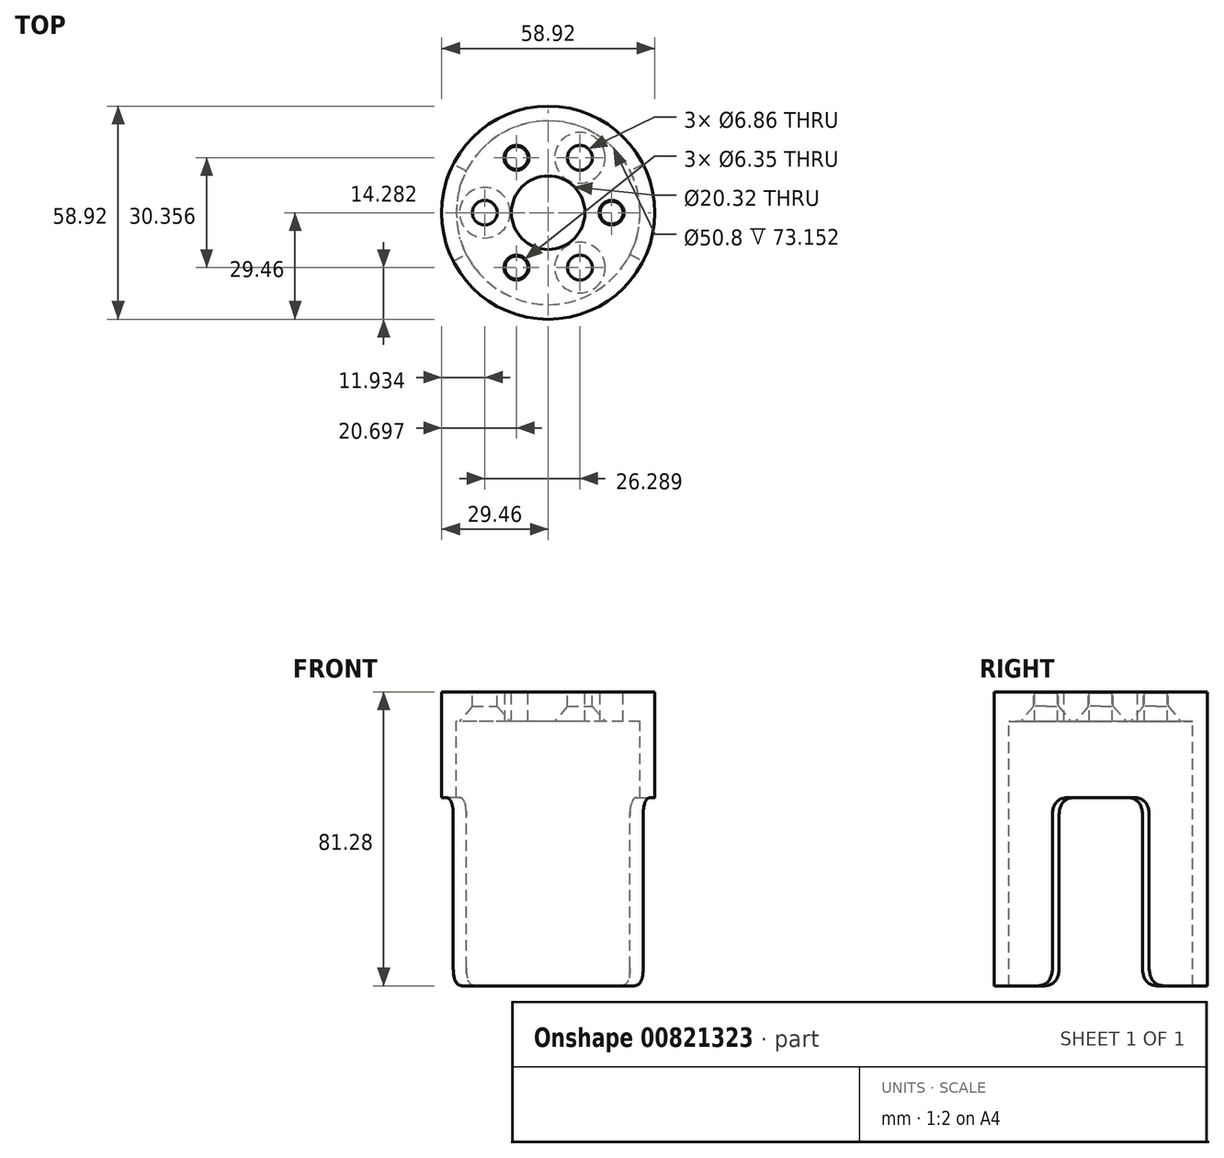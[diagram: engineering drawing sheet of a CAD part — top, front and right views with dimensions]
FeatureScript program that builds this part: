
annotation { "Feature Type Name" : "Feature", "Feature Type Description" : "" }
export const myFeature = defineFeature(function(context is Context, id is Id, definition is map)
    precondition{}
    {
        {
            var Q0;
            Q0=qCreatedBy(makeId("Top.planeOp"),FACE);
            var sketch = newSketch(context, id + "F0", { "sketchPlane" : qUnion([Q0])});
            skCircle(sketch, "E0", {"center": v(0, 0) * mm, "radius": 17.53 * mm, "construction": true});
            skCircle(sketch, "E1", {"center": v(0, 0) * mm, "radius": 10.16 * mm});
            skCircle(sketch, "E2", {"center": v(0, 0) * mm, "radius": 29.46 * mm});
            skCircle(sketch, "E3", {"center": v(17.53, 0) * mm, "radius": 3.18 * mm});
            skCircle(sketch, "E4", {"center": v(-17.53, 0) * mm, "radius": 3.43 * mm});
            skCircle(sketch, "E5.1.0", {"center": v(-8.76, 15.18) * mm, "radius": 3.18 * mm});
            skCircle(sketch, "E5.2.0", {"center": v(-8.76, -15.18) * mm, "radius": 3.18 * mm});
            skCircle(sketch, "E6.1.0", {"center": v(8.76, -15.18) * mm, "radius": 3.43 * mm});
            skCircle(sketch, "E6.2.0", {"center": v(8.76, 15.18) * mm, "radius": 3.43 * mm});
            skSolve(sketch);
        }
        {
            var Q0;
            Q0=makeQuery(id+"F0.imprint","IMPRINT",FACE,{"disambiguationData":[TD([[makeQuery(id+"F0.imprint","IMPRINT",EDGE,{"derivedFrom":sQuery(id+"F0.wireOp",EDGE,"E1")}),-1.0]])]});
            extrude(context, id + "F1", {"entities" : qUnion([Q0]), "oppositeDirection" : true, "depth" : 81.28 * mm, "offsetDistance" : 25.4 * mm});
        }
        {
            var Q0;
            Q0=qCreatedBy(makeId("Top.planeOp"),FACE);
            cPlane(context, id + "F2", {"entities" : qUnion([Q0]), "cplaneType" : CPlaneType.OFFSET, "offset" : 8.13 * mm, "oppositeDirection" : true, "width" : 152.4 * mm, "height" : 152.4 * mm});
        }
        {
            var Q0;
            Q0=qCreatedBy(id+"F2.planeOp",FACE);
            var sketch = newSketch(context, id + "F3", { "sketchPlane" : qUnion([Q0])});
            skCircle(sketch, "E7", {"center": v(0, 0) * mm, "radius": 25.4 * mm});
            skSolve(sketch);
        }
        {
            var Q0;
            Q0=makeQuery(id+"F3.imprint","IMPRINT",FACE,{"disambiguationData":[TD([[makeQuery(id+"F3.imprint","IMPRINT",EDGE,{"derivedFrom":sQuery(id+"F3.wireOp",EDGE,"E7")}),1.0]])]});
            extrude(context, id + "F4", {"entities" : qUnion([Q0]), "operationType" : NewBodyOperationType.REMOVE, "endBound" : BoundingType.THROUGH_ALL, "oppositeDirection" : true, "depth" : 25.4 * mm, "offsetDistance" : 25.4 * mm});
        }
        {
            var Q0;
            Q0=qCreatedBy(makeId("Top.planeOp"),FACE);
            cPlane(context, id + "F5", {"entities" : qUnion([Q0]), "cplaneType" : CPlaneType.OFFSET, "offset" : 29.2 * mm, "oppositeDirection" : true, "width" : 152.4 * mm, "height" : 152.4 * mm});
        }
        {
            var Q0;
            Q0=qCreatedBy(id+"F5.planeOp",FACE);
            var sketch = newSketch(context, id + "F6", { "sketchPlane" : qUnion([Q0])});
            skCircle(sketch, "E8", {"center": v(0, 0) * mm, "radius": 29.46 * mm, "construction": true});
            skCircle(sketch, "E9", {"center": v(0, 0) * mm, "radius": 25.4 * mm, "construction": true});
            skPoint(sketch, "E10", {"position": v(-22.63, 11.53) * mm});
            skPoint(sketch, "E11", {"position": v(-22.63, -11.53) * mm});
            skLineSegment(sketch, "E12", {"start": v(-26.25, 13.38) * mm, "end": v(26.25, -13.38) * mm, "construction": true});
            skLineSegment(sketch, "E13", {"start": v(26.25, 13.38) * mm, "end": v(-26.25, -13.38) * mm, "construction": true});
            skLineSegment(sketch, "E14", {"start": v(-22.63, 11.53) * mm, "end": v(-22.63, -11.53) * mm});
            skLineSegment(sketch, "E15", {"start": v(-22.63, 11.53) * mm, "end": v(-26.25, 13.38) * mm});
            skLineSegment(sketch, "E16", {"start": v(-22.63, -11.53) * mm, "end": v(-26.25, -13.38) * mm});
            skPoint(sketch, "E17", {"position": v(-29.46, 0) * mm});
            skArc(sketch, "E18", {"start": v(-26.25, 13.38) * mm, "mid": v(-29.46, 0) * mm, "end": v(-26.25, -13.38) * mm});
            skPoint(sketch, "E19", {"position": v(22.63, 11.53) * mm});
            skPoint(sketch, "E20", {"position": v(22.63, -11.53) * mm});
            skLineSegment(sketch, "E21", {"start": v(26.25, 13.38) * mm, "end": v(22.63, 11.53) * mm});
            skLineSegment(sketch, "E22", {"start": v(22.63, 11.53) * mm, "end": v(22.63, -11.53) * mm});
            skLineSegment(sketch, "E23", {"start": v(22.63, -11.53) * mm, "end": v(26.25, -13.38) * mm});
            skPoint(sketch, "E24", {"position": v(29.46, 0) * mm});
            skArc(sketch, "E25", {"start": v(26.25, -13.38) * mm, "mid": v(29.46, 0) * mm, "end": v(26.25, 13.38) * mm});
            skSolve(sketch);
        }
        {
            var Q0;
            Q0 = qSketchRegion(id + "F6", true);
            extrude(context, id + "F7", {"entities" : qUnion([Q0]), "operationType" : NewBodyOperationType.REMOVE, "endBound" : BoundingType.THROUGH_ALL, "oppositeDirection" : true, "depth" : 25.4 * mm, "offsetDistance" : 25.4 * mm});
        }
        {
            var Q0;
            Q0=makeQuery(id+"F7.boolean.opBoolean","INTERSECT",EDGE,{"derivedFrom":[makeQuery(id+"F1.opExtrude","CAP_FACE",FACE,{"disambiguationData":[OSD([sQuery(id+"F0.wireOp",EDGE,"E1"),sQuery(id+"F0.wireOp",EDGE,"E2"),sQuery(id+"F0.wireOp",EDGE,"E3"),sQuery(id+"F0.wireOp",EDGE,"E4"),sQuery(id+"F0.wireOp",EDGE,"E5.1.0"),sQuery(id+"F0.wireOp",EDGE,"E5.2.0"),sQuery(id+"F0.wireOp",EDGE,"E6.1.0"),sQuery(id+"F0.wireOp",EDGE,"E6.2.0")])],"isStart":false}),makeQuery(id+"F7.opExtrude","SWEPT_FACE",FACE,{"disambiguationData":[OSD([sQuery(id+"F6.wireOp",EDGE,"E23")])]})]});
            var Q1;
            Q1=makeQuery(id+"F7.boolean.opBoolean","INTERSECT",EDGE,{"derivedFrom":[makeQuery(id+"F1.opExtrude","CAP_FACE",FACE,{"disambiguationData":[OSD([sQuery(id+"F0.wireOp",EDGE,"E1"),sQuery(id+"F0.wireOp",EDGE,"E2"),sQuery(id+"F0.wireOp",EDGE,"E3"),sQuery(id+"F0.wireOp",EDGE,"E4"),sQuery(id+"F0.wireOp",EDGE,"E5.1.0"),sQuery(id+"F0.wireOp",EDGE,"E5.2.0"),sQuery(id+"F0.wireOp",EDGE,"E6.1.0"),sQuery(id+"F0.wireOp",EDGE,"E6.2.0")])],"isStart":false}),makeQuery(id+"F7.opExtrude","SWEPT_FACE",FACE,{"disambiguationData":[OSD([sQuery(id+"F6.wireOp",EDGE,"E21")])]})]});
            var Q2;
            Q2=makeQuery(id+"F7.boolean.opBoolean","INTERSECT",EDGE,{"derivedFrom":[makeQuery(id+"F1.opExtrude","CAP_FACE",FACE,{"disambiguationData":[OSD([sQuery(id+"F0.wireOp",EDGE,"E1"),sQuery(id+"F0.wireOp",EDGE,"E2"),sQuery(id+"F0.wireOp",EDGE,"E3"),sQuery(id+"F0.wireOp",EDGE,"E4"),sQuery(id+"F0.wireOp",EDGE,"E5.1.0"),sQuery(id+"F0.wireOp",EDGE,"E5.2.0"),sQuery(id+"F0.wireOp",EDGE,"E6.1.0"),sQuery(id+"F0.wireOp",EDGE,"E6.2.0")])],"isStart":false}),makeQuery(id+"F7.opExtrude","SWEPT_FACE",FACE,{"disambiguationData":[OSD([sQuery(id+"F6.wireOp",EDGE,"E15")])]})]});
            var Q3;
            Q3=makeQuery(id+"F7.boolean.opBoolean","INTERSECT",EDGE,{"derivedFrom":[makeQuery(id+"F1.opExtrude","CAP_FACE",FACE,{"disambiguationData":[OSD([sQuery(id+"F0.wireOp",EDGE,"E1"),sQuery(id+"F0.wireOp",EDGE,"E2"),sQuery(id+"F0.wireOp",EDGE,"E3"),sQuery(id+"F0.wireOp",EDGE,"E4"),sQuery(id+"F0.wireOp",EDGE,"E5.1.0"),sQuery(id+"F0.wireOp",EDGE,"E5.2.0"),sQuery(id+"F0.wireOp",EDGE,"E6.1.0"),sQuery(id+"F0.wireOp",EDGE,"E6.2.0")])],"isStart":false}),makeQuery(id+"F7.opExtrude","SWEPT_FACE",FACE,{"disambiguationData":[OSD([sQuery(id+"F6.wireOp",EDGE,"E16")])]})]});
            fillet(context, id + "F8", {"entities" : qUnion([Q0, Q1, Q2, Q3]), "radius" : 5.08 * mm, "tangentPropagation" : true, "rho" : 0.5, "crossSection" : FilletCrossSection.CONIC, "allowEdgeOverflow" : false});
        }
        {
            var Q0;
            Q0=makeQuery(id+"F7.boolean.opBoolean","COPY",EDGE,{"derivedFrom":makeQuery(id+"F7.opExtrude","CAP_EDGE",EDGE,{"disambiguationData":[OSD([sQuery(id+"F6.wireOp",EDGE,"E16")])],"isStart":true})});
            var Q1;
            Q1=makeQuery(id+"F7.boolean.opBoolean","COPY",EDGE,{"derivedFrom":makeQuery(id+"F7.opExtrude","CAP_EDGE",EDGE,{"disambiguationData":[OSD([sQuery(id+"F6.wireOp",EDGE,"E15")])],"isStart":true})});
            var Q2;
            Q2=makeQuery(id+"F7.boolean.opBoolean","COPY",EDGE,{"derivedFrom":makeQuery(id+"F7.opExtrude","CAP_EDGE",EDGE,{"disambiguationData":[OSD([sQuery(id+"F6.wireOp",EDGE,"E23")])],"isStart":true})});
            var Q3;
            Q3=makeQuery(id+"F7.boolean.opBoolean","COPY",EDGE,{"derivedFrom":makeQuery(id+"F7.opExtrude","CAP_EDGE",EDGE,{"disambiguationData":[OSD([sQuery(id+"F6.wireOp",EDGE,"E21")])],"isStart":true})});
            fillet(context, id + "F9", {"entities" : qUnion([Q0, Q1, Q2, Q3]), "radius" : 5.08 * mm, "tangentPropagation" : true, "rho" : 0.5, "crossSection" : FilletCrossSection.CONIC, "allowEdgeOverflow" : false});
        }
        {
            var Q0;
            Q0=qCreatedBy(makeId("Top.planeOp"),FACE);
            var sketch = newSketch(context, id + "F10", { "sketchPlane" : qUnion([Q0])});
            skCircle(sketch, "E26", {"center": v(0, 0) * mm, "radius": 17.53 * mm, "construction": true});
            skCircle(sketch, "E27", {"center": v(17.53, 0) * mm, "radius": 3.43 * mm});
            skCircle(sketch, "E28.1.0", {"center": v(-8.76, 15.18) * mm, "radius": 3.43 * mm});
            skCircle(sketch, "E28.2.0", {"center": v(-8.76, -15.18) * mm, "radius": 3.43 * mm});
            skSolve(sketch);
        }
        {
            var Q0;
            Q0=makeQuery(id+"F10.imprint","IMPRINT",FACE,{"disambiguationData":[TD([[makeQuery(id+"F10.imprint","IMPRINT",EDGE,{"derivedFrom":sQuery(id+"F10.wireOp",EDGE,"E27")}),1.0]])]});
            var Q1;
            Q1=makeQuery(id+"F10.imprint","IMPRINT",FACE,{"disambiguationData":[TD([[makeQuery(id+"F10.imprint","IMPRINT",EDGE,{"derivedFrom":sQuery(id+"F10.wireOp",EDGE,"E28.1.0")}),1.0]])]});
            var Q2;
            Q2=makeQuery(id+"F10.imprint","IMPRINT",FACE,{"disambiguationData":[TD([[makeQuery(id+"F10.imprint","IMPRINT",EDGE,{"derivedFrom":sQuery(id+"F10.wireOp",EDGE,"E28.2.0")}),1.0]])]});
            extrude(context, id + "F11", {"entities" : qUnion([Q0, Q1, Q2]), "operationType" : NewBodyOperationType.REMOVE, "oppositeDirection" : true, "depth" : 2.54 * mm, "offsetDistance" : 25.4 * mm, "hasDraft" : true, "draftAngle" : 45 * degree, "draftPullDirection" : true});
        }
        {
            var Q0;
            Q0=qCreatedBy(id+"F2.planeOp",FACE);
            var sketch = newSketch(context, id + "F12", { "sketchPlane" : qUnion([Q0])});
            skCircle(sketch, "E29", {"center": v(0, 0) * mm, "radius": 17.53 * mm, "construction": true});
            skCircle(sketch, "E30", {"center": v(-17.53, 0) * mm, "radius": 6.99 * mm});
            skCircle(sketch, "E31.1.0", {"center": v(8.76, -15.18) * mm, "radius": 6.99 * mm});
            skCircle(sketch, "E31.2.0", {"center": v(8.76, 15.18) * mm, "radius": 6.99 * mm});
            skSolve(sketch);
        }
        {
            var Q0;
            Q0=makeQuery(id+"F12.imprint","IMPRINT",FACE,{"disambiguationData":[TD([[makeQuery(id+"F12.imprint","IMPRINT",EDGE,{"derivedFrom":sQuery(id+"F12.wireOp",EDGE,"E30")}),1.0]])]});
            var Q1;
            Q1=makeQuery(id+"F12.imprint","IMPRINT",FACE,{"disambiguationData":[TD([[makeQuery(id+"F12.imprint","IMPRINT",EDGE,{"derivedFrom":sQuery(id+"F12.wireOp",EDGE,"E31.1.0")}),1.0]])]});
            var Q2;
            Q2=makeQuery(id+"F12.imprint","IMPRINT",FACE,{"disambiguationData":[TD([[makeQuery(id+"F12.imprint","IMPRINT",EDGE,{"derivedFrom":sQuery(id+"F12.wireOp",EDGE,"E31.2.0")}),1.0]])]});
            extrude(context, id + "F13", {"entities" : qUnion([Q0, Q1, Q2]), "operationType" : NewBodyOperationType.REMOVE, "endBound" : BoundingType.THROUGH_ALL, "depth" : 6.35 * mm, "offsetDistance" : 25.4 * mm, "hasDraft" : true, "draftAngle" : 41 * degree, "draftPullDirection" : true});
        }
    });
